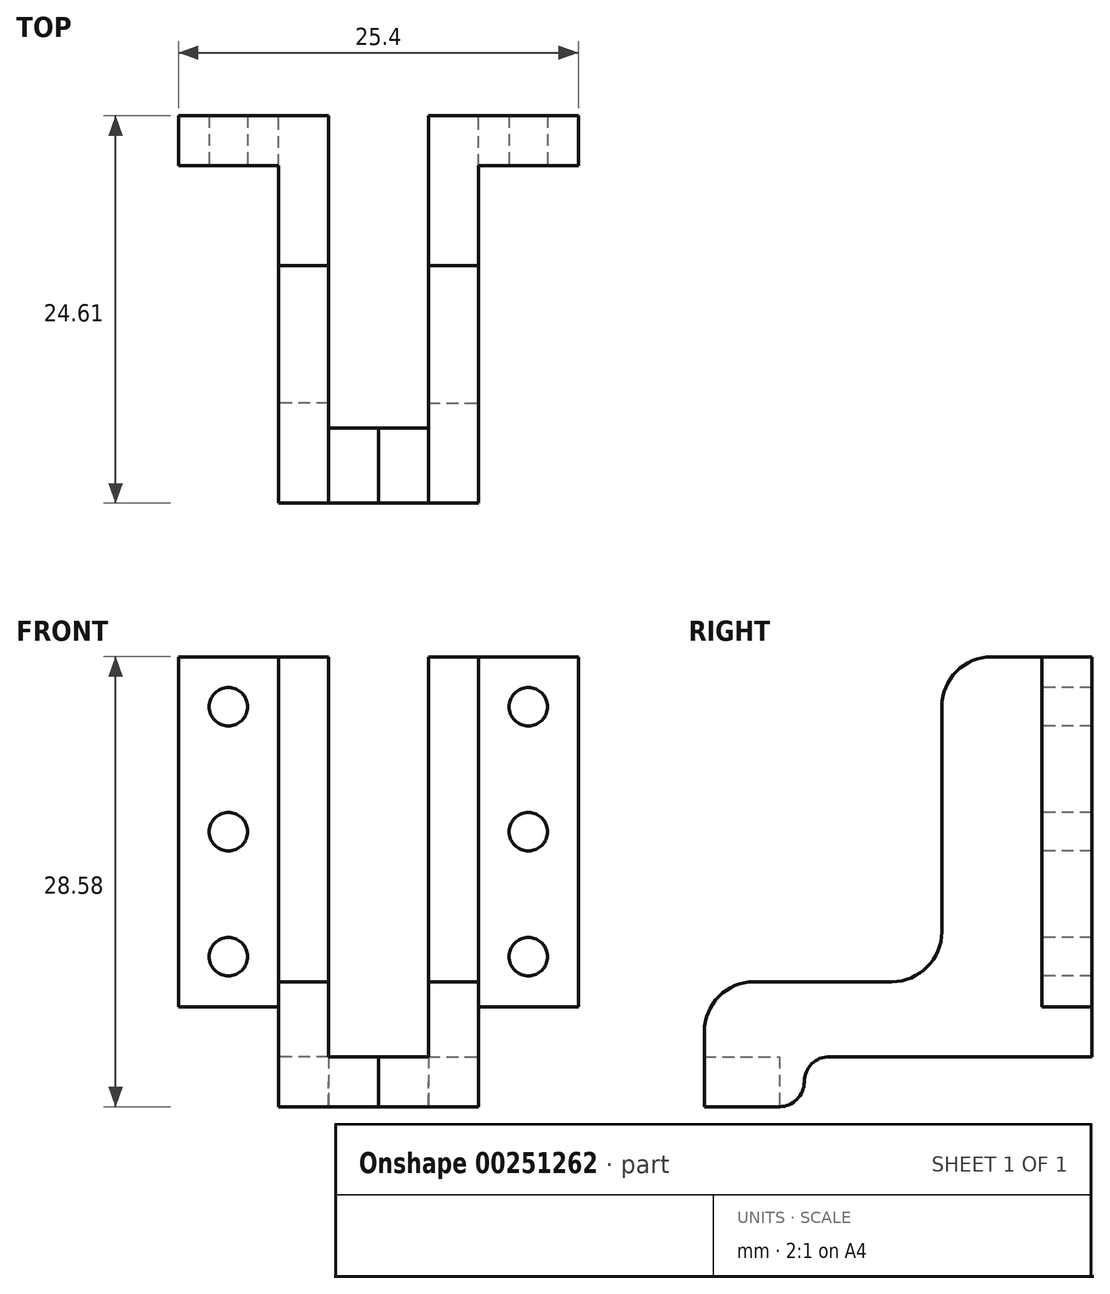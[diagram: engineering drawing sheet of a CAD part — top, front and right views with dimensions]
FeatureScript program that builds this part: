
annotation { "Feature Type Name" : "Feature", "Feature Type Description" : "" }
export const myFeature = defineFeature(function(context is Context, id is Id, definition is map)
    precondition{}
    {
        {
            var Q0;
            Q0=qCreatedBy(makeId("Right.planeOp"),FACE);
            var sketch = newSketch(context, id + "F0", { "sketchPlane" : qUnion([Q0])});
            skLineSegment(sketch, "E0", {"start": v(31.33, 44.33) * mm, "end": v(37.68, 44.33) * mm});
            skLineSegment(sketch, "E1", {"start": v(37.68, 44.33) * mm, "end": v(37.68, 18.93) * mm});
            skLineSegment(sketch, "E2", {"start": v(37.68, 18.93) * mm, "end": v(21, 18.93) * mm});
            skLineSegment(sketch, "E3", {"start": v(19.42, 17.34) * mm, "end": v(19.42, 17.34) * mm});
            skLineSegment(sketch, "E4", {"start": v(17.83, 15.75) * mm, "end": v(13.07, 15.75) * mm});
            skLineSegment(sketch, "E5", {"start": v(13.07, 15.75) * mm, "end": v(13.07, 20.51) * mm});
            skLineSegment(sketch, "E6", {"start": v(16.24, 23.69) * mm, "end": v(24.98, 23.69) * mm});
            skLineSegment(sketch, "E7", {"start": v(28.15, 26.86) * mm, "end": v(28.15, 41.15) * mm});
            skPoint(sketch, "E8.orphan", {"position": v(13.07, 15.75) * mm});
            skPoint(sketch, "E9.orphan", {"position": v(13.07, 22.67) * mm});
            skPoint(sketch, "E10.visualSharp", {"position": v(28.15, 44.33) * mm});
            skArc(sketch, "E10.filletArc", {"start": v(31.33, 44.33) * mm, "mid": v(29.08, 43.4) * mm, "end": v(28.15, 41.15) * mm});
            skPoint(sketch, "E11.visualSharp", {"position": v(28.15, 23.69) * mm});
            skArc(sketch, "E11.filletArc", {"start": v(24.98, 23.69) * mm, "mid": v(27.22, 24.62) * mm, "end": v(28.15, 26.86) * mm});
            skPoint(sketch, "E12.visualSharp", {"position": v(13.07, 23.69) * mm});
            skArc(sketch, "E12.filletArc", {"start": v(16.24, 23.69) * mm, "mid": v(14, 22.76) * mm, "end": v(13.07, 20.51) * mm});
            skPoint(sketch, "E13.visualSharp", {"position": v(19.42, 18.93) * mm});
            skArc(sketch, "E13.filletArc", {"start": v(21, 18.93) * mm, "mid": v(19.88, 18.46) * mm, "end": v(19.42, 17.34) * mm});
            skPoint(sketch, "E14.visualSharp", {"position": v(19.42, 15.75) * mm});
            skArc(sketch, "E14.filletArc", {"start": v(17.83, 15.75) * mm, "mid": v(18.95, 16.22) * mm, "end": v(19.42, 17.34) * mm});
            skSolve(sketch);
        }
        {
            var Q0;
            Q0 = qSketchRegion(id + "F0", true);
            extrude(context, id + "F1", {"entities" : qUnion([Q0]), "depth" : 3.17 * mm});
        }
        {
            var Q0;
            Q0=makeQuery(id+"F1.opExtrude","CAP_FACE",FACE,{"disambiguationData":[OSD([sQuery(id+"F0.wireOp",EDGE,"E0"),sQuery(id+"F0.wireOp",EDGE,"E1"),sQuery(id+"F0.wireOp",EDGE,"E2"),sQuery(id+"F0.wireOp",EDGE,"E4"),sQuery(id+"F0.wireOp",EDGE,"E5"),sQuery(id+"F0.wireOp",EDGE,"E6"),sQuery(id+"F0.wireOp",EDGE,"E7"),sQuery(id+"F0.wireOp",EDGE,"E10.filletArc"),sQuery(id+"F0.wireOp",EDGE,"E11.filletArc"),sQuery(id+"F0.wireOp",EDGE,"E12.filletArc"),sQuery(id+"F0.wireOp",EDGE,"E13.filletArc"),sQuery(id+"F0.wireOp",EDGE,"E14.filletArc")])],"isStart":false});
            var sketch = newSketch(context, id + "F2", { "sketchPlane" : qUnion([Q0])});
            skLineSegment(sketch, "E15", {"start": v(13.07, 18.93) * mm, "end": v(17.83, 18.93) * mm});
            skLineSegment(sketch, "E16", {"start": v(17.83, 18.93) * mm, "end": v(17.83, 15.75) * mm});
            skSolve(sketch);
        }
        {
            var Q0;
            Q0 = qSketchRegion(id + "F2", true);
            var Q1;
            {var subQ0=sQuery(id+"F2.wireOp",EDGE,"E15");Q1=makeQuery(id+"F2.imprint","IMPRINT",FACE,{"disambiguationData":[TD([[makeQuery(id+"F2.imprint","IMPRINT",EDGE,{"derivedFrom":subQ0}),-1.0]])]});}
            extrude(context, id + "F3", {"entities" : qUnion([Q0, Q1]), "operationType" : NewBodyOperationType.ADD, "depth" : 3.17 * mm});
        }
        {
            var Q0;
            Q0=makeQuery(id+"F1.opExtrude","CAP_FACE",FACE,{"disambiguationData":[OSD([sQuery(id+"F0.wireOp",EDGE,"E0"),sQuery(id+"F0.wireOp",EDGE,"E1"),sQuery(id+"F0.wireOp",EDGE,"E2"),sQuery(id+"F0.wireOp",EDGE,"E4"),sQuery(id+"F0.wireOp",EDGE,"E5"),sQuery(id+"F0.wireOp",EDGE,"E6"),sQuery(id+"F0.wireOp",EDGE,"E7"),sQuery(id+"F0.wireOp",EDGE,"E10.filletArc"),sQuery(id+"F0.wireOp",EDGE,"E11.filletArc"),sQuery(id+"F0.wireOp",EDGE,"E12.filletArc"),sQuery(id+"F0.wireOp",EDGE,"E13.filletArc"),sQuery(id+"F0.wireOp",EDGE,"E14.filletArc")])],"isStart":true});
            var sketch = newSketch(context, id + "F4", { "sketchPlane" : qUnion([Q0])});
            skLineSegment(sketch, "E17", {"start": v(-34.5, 44.33) * mm, "end": v(-34.5, 22.1) * mm});
            skLineSegment(sketch, "E18", {"start": v(-34.5, 22.1) * mm, "end": v(-37.68, 22.1) * mm});
            skSolve(sketch);
        }
        {
            var Q0;
            {var subQ0=sQuery(id+"F4.wireOp",EDGE,"E17");Q0=makeQuery(id+"F4.imprint","IMPRINT",FACE,{"disambiguationData":[TD([[makeQuery(id+"F4.imprint","IMPRINT",EDGE,{"derivedFrom":subQ0}),-1.0]])]});}
            extrude(context, id + "F5", {"entities" : qUnion([Q0]), "operationType" : NewBodyOperationType.ADD, "depth" : 6.35 * mm});
        }
        {
            var Q0;
            Q0=makeQuery(id+"F5.opExtrude","SWEPT_FACE",FACE,{"disambiguationData":[OSD([sQuery(id+"F4.wireOp",EDGE,"E17")])]});
            var sketch = newSketch(context, id + "F6", { "sketchPlane" : qUnion([Q0])});
            skCircle(sketch, "E19", {"center": v(-3.18, 41.15) * mm, "radius": 1.22 * mm});
            skCircle(sketch, "E20", {"center": v(-3.18, 33.21) * mm, "radius": 1.22 * mm});
            skCircle(sketch, "E21", {"center": v(-3.18, 25.28) * mm, "radius": 1.22 * mm});
            skSolve(sketch);
        }
        {
            var Q0;
            Q0=makeQuery(id+"F6.imprint","IMPRINT",FACE,{"disambiguationData":[TD([[makeQuery(id+"F6.imprint","IMPRINT",EDGE,{"derivedFrom":sQuery(id+"F6.wireOp",EDGE,"E19")}),1.0]])]});
            var Q1;
            Q1=makeQuery(id+"F6.imprint","IMPRINT",FACE,{"disambiguationData":[TD([[makeQuery(id+"F6.imprint","IMPRINT",EDGE,{"derivedFrom":sQuery(id+"F6.wireOp",EDGE,"E20")}),1.0]])]});
            var Q2;
            Q2=makeQuery(id+"F6.imprint","IMPRINT",FACE,{"disambiguationData":[TD([[makeQuery(id+"F6.imprint","IMPRINT",EDGE,{"derivedFrom":sQuery(id+"F6.wireOp",EDGE,"E21")}),1.0]])]});
            extrude(context, id + "F7", {"entities" : qUnion([Q0, Q1, Q2]), "operationType" : NewBodyOperationType.REMOVE, "oppositeDirection" : true, "depth" : 25.4 * mm});
        }
        {
            var Q0;
            Q0=makeQuery(id+"F1.opExtrude","SWEPT_BODY",BODY,{"disambiguationData":[OSD([sQuery(id+"F0.wireOp",EDGE,"E0"),sQuery(id+"F0.wireOp",EDGE,"E1"),sQuery(id+"F0.wireOp",EDGE,"E2"),sQuery(id+"F0.wireOp",EDGE,"E4"),sQuery(id+"F0.wireOp",EDGE,"E5"),sQuery(id+"F0.wireOp",EDGE,"E6"),sQuery(id+"F0.wireOp",EDGE,"E7"),sQuery(id+"F0.wireOp",EDGE,"E10.filletArc"),sQuery(id+"F0.wireOp",EDGE,"E11.filletArc"),sQuery(id+"F0.wireOp",EDGE,"E12.filletArc"),sQuery(id+"F0.wireOp",EDGE,"E13.filletArc"),sQuery(id+"F0.wireOp",EDGE,"E14.filletArc")])]});
            var Q1;
            Q1=makeQuery(id+"F3.opExtrude","CAP_FACE",FACE,{"disambiguationData":[OSD([sQuery(id+"F0.wireOp",EDGE,"E4"),sQuery(id+"F0.wireOp",EDGE,"E5"),sQuery(id+"F2.wireOp",EDGE,"E15"),sQuery(id+"F2.wireOp",EDGE,"E16")])],"isStart":false});
            mirror(context, id + "F8", {"entities" : qUnion([Q0]), "mirrorPlane" : qUnion([Q1])});
        }
    });
